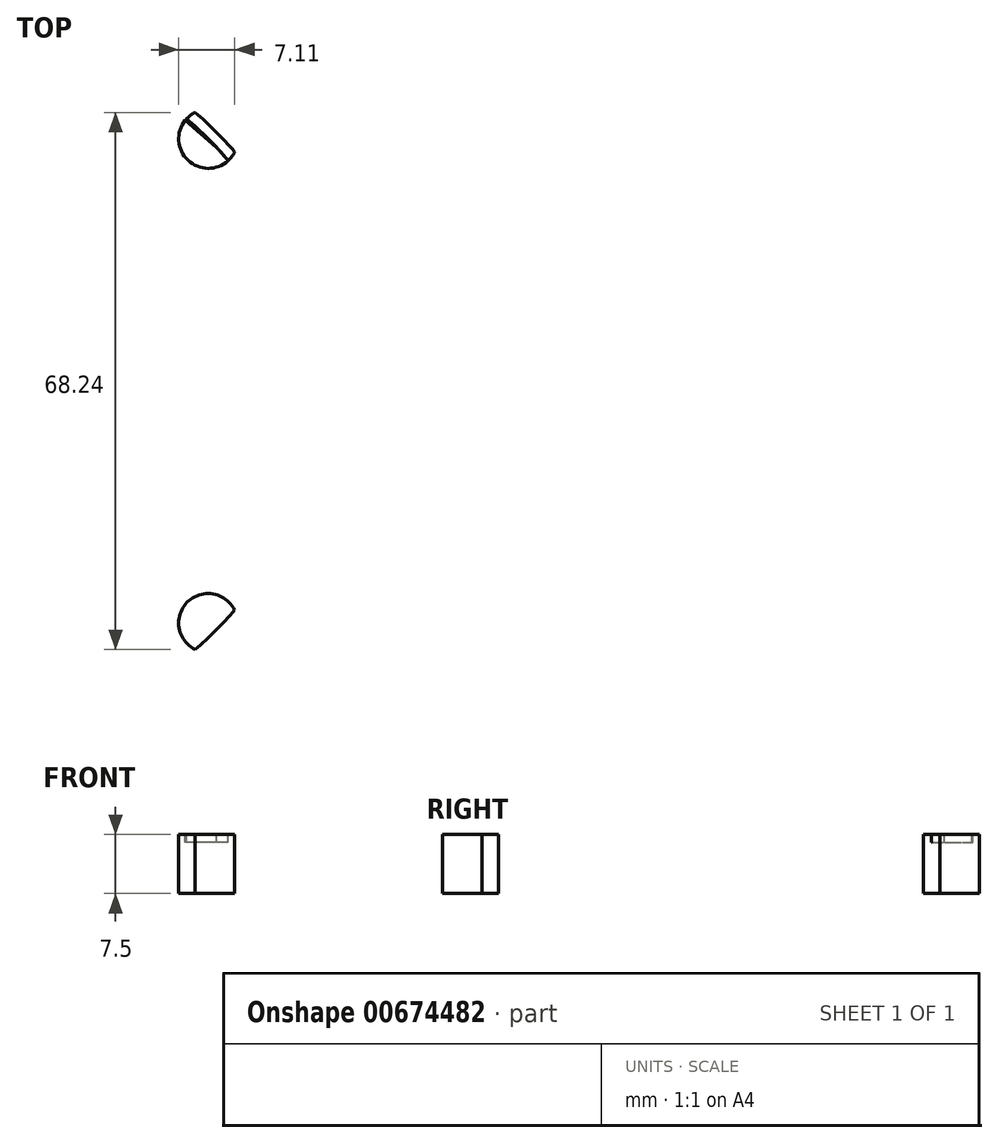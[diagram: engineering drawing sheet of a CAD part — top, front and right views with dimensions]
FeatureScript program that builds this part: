
annotation { "Feature Type Name" : "Feature", "Feature Type Description" : "" }
export const myFeature = defineFeature(function(context is Context, id is Id, definition is map)
    precondition{}
    {
        {
            var Q0;
            Q0=qCreatedBy(makeId("Top.planeOp"),FACE);
            var sketch = newSketch(context, id + "F0", { "sketchPlane" : qUnion([Q0])});
            skCircle(sketch, "E0", {"center": v(0, 0) * mm, "radius": 43.5 * mm, "construction": true});
            skLineSegment(sketch, "E1", {"start": v(0, 0) * mm, "end": v(30.76, 30.76) * mm, "construction": true});
            skCircle(sketch, "E2", {"center": v(30.76, 30.76) * mm, "radius": 3.75 * mm});
            skCircle(sketch, "E3.1.0", {"center": v(-30.76, 30.76) * mm, "radius": 3.75 * mm});
            skCircle(sketch, "E3.2.0", {"center": v(-30.76, -30.76) * mm, "radius": 3.75 * mm});
            skCircle(sketch, "E3.3.0", {"center": v(30.76, -30.76) * mm, "radius": 3.75 * mm});
            skLineSegment(sketch, "E4", {"start": v(0, 0) * mm, "end": v(30.76, -30.76) * mm, "construction": true});
            skSolve(sketch);
        }
        {
            var Q0;
            Q0=qCreatedBy(makeId("Top.planeOp"),FACE);
            var sketch = newSketch(context, id + "F1", { "sketchPlane" : qUnion([Q0])});
            skLineSegment(sketch, "E5", {"start": v(4.74, 19.78) * mm, "end": v(15.3, 42.68) * mm});
            skLineSegment(sketch, "E6", {"start": v(4.74, -19.78) * mm, "end": v(15.3, -42.68) * mm});
            skLineSegment(sketch, "E7", {"start": v(0, 0) * mm, "end": v(0, 47.02) * mm, "construction": true});
            skLineSegment(sketch, "E8", {"start": v(0, 0) * mm, "end": v(0, -46.33) * mm, "construction": true});
            skPoint(sketch, "E9.visualSharp", {"position": v(16.93, 46.23) * mm});
            skArc(sketch, "E9.filletArc", {"start": v(22.32, 38.88) * mm, "mid": v(20.83, 44.52) * mm, "end": v(15.3, 42.68) * mm});
            skPoint(sketch, "E10.visualSharp", {"position": v(4.23, 18.67) * mm});
            skArc(sketch, "E10.filletArc", {"start": v(4.74, 19.78) * mm, "mid": v(6.54, 14.55) * mm, "end": v(11.85, 16.11) * mm});
            skPoint(sketch, "E11.visualSharp", {"position": v(4.23, -18.67) * mm});
            skArc(sketch, "E11.filletArc", {"start": v(11.85, -16.11) * mm, "mid": v(6.54, -14.55) * mm, "end": v(4.74, -19.78) * mm});
            skPoint(sketch, "E12.visualSharp", {"position": v(16.93, -46.23) * mm});
            skArc(sketch, "E12.filletArc", {"start": v(15.3, -42.68) * mm, "mid": v(20.83, -44.52) * mm, "end": v(22.32, -38.88) * mm});
            skLineSegment(sketch, "E13", {"start": v(0, 0) * mm, "end": v(50, 0) * mm, "construction": true});
            skArc(sketch, "E14", {"start": v(11.85, 16.11) * mm, "mid": v(20, 0) * mm, "end": v(11.85, -16.11) * mm});
            skArc(sketch, "E15", {"start": v(22.32, 38.88) * mm, "mid": v(44.84, 0) * mm, "end": v(22.32, -38.88) * mm});
            skLineSegment(sketch, "E16", {"start": v(22.32, 38.88) * mm, "end": v(22.32, 0) * mm, "construction": true});
            skLineSegment(sketch, "E17", {"start": v(22.32, 0) * mm, "end": v(22.32, -38.88) * mm, "construction": true});
            skLineSegment(sketch, "E18", {"start": v(0, 42.68) * mm, "end": v(15.3, 42.68) * mm, "construction": true});
            skLineSegment(sketch, "E19", {"start": v(0, -42.68) * mm, "end": v(15.3, -42.68) * mm, "construction": true});
            skSolve(sketch);
        }
        {
            var Q0;
            Q0=makeQuery(id+"F1.imprint","IMPRINT",FACE,{"disambiguationData":[TD([[makeQuery(id+"F1.imprint","IMPRINT",EDGE,{"derivedFrom":sQuery(id+"F1.wireOp",EDGE,"E5")}),-1.0]])]});
            extrude(context, id + "F2", {"entities" : qUnion([Q0]), "depth" : 3 * mm, "offsetDistance" : 25 * mm});
        }
        {
            var Q0;
            Q0=makeQuery(id+"F0.imprint","IMPRINT",FACE,{"disambiguationData":[TD([[makeQuery(id+"F0.imprint","IMPRINT",EDGE,{"derivedFrom":sQuery(id+"F0.wireOp",EDGE,"E2")}),1.0]])]});
            var Q1;
            Q1=makeQuery(id+"F0.imprint","IMPRINT",FACE,{"disambiguationData":[TD([[makeQuery(id+"F0.imprint","IMPRINT",EDGE,{"derivedFrom":sQuery(id+"F0.wireOp",EDGE,"E3.3.0")}),1.0]])]});
            extrude(context, id + "F3", {"entities" : qUnion([Q0, Q1]), "operationType" : NewBodyOperationType.REMOVE, "depth" : 25 * mm, "offsetDistance" : 25 * mm});
        }
        {
            var Q0;
            Q0=makeQuery(id+"F2.opExtrude","CAP_FACE",FACE,{"disambiguationData":[OSD([sQuery(id+"F1.wireOp",EDGE,"KiuFZQME-wWnU-ktu5-Gd9x-qji5TMNZz2fd"),sQuery(id+"F1.wireOp",EDGE,"G5eraXv0-ftC7-V2Hx-4i3N-1R2XA50WnSdq"),sQuery(id+"F1.wireOp",EDGE,"E5"),sQuery(id+"F1.wireOp",EDGE,"E6"),sQuery(id+"F1.wireOp",EDGE,"57560024-62e8-479f-91f4-8b403f4d0ad7.filletArc"),sQuery(id+"F1.wireOp",EDGE,"ddf71622-e854-4fa8-aca5-087326283111.filletArc"),sQuery(id+"F1.wireOp",EDGE,"85b82a5b-4425-4996-801d-5779b438c59f.filletArc"),sQuery(id+"F1.wireOp",EDGE,"35c327b1-5974-4460-b54d-dc77ba413df5.filletArc")])],"isStart":false});
            var sketch = newSketch(context, id + "F4", { "sketchPlane" : qUnion([Q0])});
            skArc(sketch, "E20", {"start": v(13.6, 20.4) * mm, "mid": v(24.52, 0) * mm, "end": v(13.6, -20.4) * mm});
            skArc(sketch, "E21", {"start": v(16.92, 25.4) * mm, "mid": v(30.52, 0) * mm, "end": v(16.92, -25.4) * mm});
            skLineSegment(sketch, "E22", {"start": v(0, 0) * mm, "end": v(16.92, -25.4) * mm, "construction": true});
            skLineSegment(sketch, "E23", {"start": v(0, 0) * mm, "end": v(16.92, 25.4) * mm, "construction": true});
            skLineSegment(sketch, "E24", {"start": v(13.6, 20.4) * mm, "end": v(13.6, 0) * mm, "construction": true});
            skLineSegment(sketch, "E25", {"start": v(13.6, 0) * mm, "end": v(13.6, -20.4) * mm, "construction": true});
            skArc(sketch, "E26", {"start": v(13.6, 20.4) * mm, "mid": v(12.76, 24.57) * mm, "end": v(16.92, 25.4) * mm});
            skArc(sketch, "E27", {"start": v(13.6, -20.4) * mm, "mid": v(12.76, -24.57) * mm, "end": v(16.92, -25.4) * mm});
            skSolve(sketch);
        }
        {
            var Q0;
            Q0=qSketchRegion(id+"F4",true);
            extrude(context, id + "F5", {"entities" : qUnion([Q0]), "operationType" : NewBodyOperationType.REMOVE, "oppositeDirection" : true, "depth" : 25 * mm, "offsetDistance" : 25 * mm});
        }
        {
            var Q0;
            Q0=makeQuery(id+"F2.opExtrude","CAP_FACE",FACE,{"disambiguationData":[OSD([sQuery(id+"F1.wireOp",EDGE,"E5"),sQuery(id+"F1.wireOp",EDGE,"E6"),sQuery(id+"F1.wireOp",EDGE,"E9.filletArc"),sQuery(id+"F1.wireOp",EDGE,"E10.filletArc"),sQuery(id+"F1.wireOp",EDGE,"E11.filletArc"),sQuery(id+"F1.wireOp",EDGE,"E12.filletArc"),sQuery(id+"F1.wireOp",EDGE,"E14"),sQuery(id+"F1.wireOp",EDGE,"E15")])],"isStart":true});
            var sketch = newSketch(context, id + "F6", { "sketchPlane" : qUnion([Q0])});
            skArc(sketch, "E28", {"start": v(22.32, -38.88) * mm, "mid": v(44.66, 3.97) * mm, "end": v(15.12, 42.21) * mm});
            skArc(sketch, "E29", {"start": v(11.26, 24.36) * mm, "mid": v(26.84, 0) * mm, "end": v(11.26, -24.36) * mm});
            skLineSegment(sketch, "E30", {"start": v(9.3, -29.67) * mm, "end": v(15.3, -42.68) * mm});
            skLineSegment(sketch, "E31", {"start": v(9.3, 29.67) * mm, "end": v(15.3, 42.68) * mm});
            skArc(sketch, "E32", {"start": v(15.3, -42.68) * mm, "mid": v(20.83, -44.52) * mm, "end": v(22.32, -38.88) * mm});
            skArc(sketch, "E33", {"start": v(15.12, 42.21) * mm, "mid": v(14.97, 42.54) * mm, "end": v(15.3, 42.68) * mm});
            skPoint(sketch, "E34.visualSharp", {"position": v(7.5, -25.77) * mm});
            skArc(sketch, "E34.filletArc", {"start": v(11.26, -24.36) * mm, "mid": v(9.18, -26.61) * mm, "end": v(9.3, -29.67) * mm});
            skPoint(sketch, "E35.visualSharp", {"position": v(7.5, 25.77) * mm});
            skArc(sketch, "E35.filletArc", {"start": v(9.3, 29.67) * mm, "mid": v(9.18, 26.61) * mm, "end": v(11.26, 24.36) * mm});
            skSolve(sketch);
        }
        {
            var Q0;
            Q0=makeQuery(id+"F6.imprint","IMPRINT",FACE,{"disambiguationData":[TD([[makeQuery(id+"F6.imprint","IMPRINT",EDGE,{"derivedFrom":sQuery(id+"F6.wireOp",EDGE,"E28")}),1.0]])]});
            extrude(context, id + "F7", {"entities" : qUnion([Q0]), "depth" : 7.5 * mm, "offsetDistance" : 25 * mm});
        }
        {
            var Q0;
            Q0=makeQuery(id+"F2.opExtrude","SWEPT_BODY",BODY,{"disambiguationData":[OSD([sQuery(id+"F1.wireOp",EDGE,"E5"),sQuery(id+"F1.wireOp",EDGE,"E6"),sQuery(id+"F1.wireOp",EDGE,"E9.filletArc"),sQuery(id+"F1.wireOp",EDGE,"E10.filletArc"),sQuery(id+"F1.wireOp",EDGE,"E11.filletArc"),sQuery(id+"F1.wireOp",EDGE,"E12.filletArc"),sQuery(id+"F1.wireOp",EDGE,"E14"),sQuery(id+"F1.wireOp",EDGE,"E15")])]});
            deleteBodies(context, id + "F8", {"entities" : qUnion([Q0])});
        }
        {
            var Q0;
            Q0=makeQuery(id+"F7.opExtrude","CAP_FACE",FACE,{"disambiguationData":[OSD([sQuery(id+"F0.wireOp",EDGE,"E2"),sQuery(id+"F0.wireOp",EDGE,"E3.3.0"),sQuery(id+"F6.wireOp",EDGE,"E28"),sQuery(id+"F6.wireOp",EDGE,"E29"),sQuery(id+"F6.wireOp",EDGE,"E30"),sQuery(id+"F6.wireOp",EDGE,"E31"),sQuery(id+"F6.wireOp",EDGE,"E32"),sQuery(id+"F6.wireOp",EDGE,"E33"),sQuery(id+"F6.wireOp",EDGE,"E34.filletArc"),sQuery(id+"F6.wireOp",EDGE,"E35.filletArc")])],"isStart":true});
            var sketch = newSketch(context, id + "F9", { "sketchPlane" : qUnion([Q0])});
            skArc(sketch, "E36", {"start": v(31.8, 29.67) * mm, "mid": v(33.09, 28.23) * mm, "end": v(34.3, 26.73) * mm});
            skArc(sketch, "E37", {"start": v(25.11, 35.53) * mm, "mid": v(30.24, 31.28) * mm, "end": v(34.66, 26.3) * mm});
            skCircle(sketch, "E38", {"center": v(30.76, 30.76) * mm, "radius": 3.75 * mm, "construction": true});
            skLineSegment(sketch, "E39", {"start": v(30.75, 30.76) * mm, "end": v(30.76, 30.76) * mm, "construction": true});
            skLineSegment(sketch, "E40", {"start": v(30.76, 30.76) * mm, "end": v(30.77, 30.76) * mm, "construction": true});
            skLineSegment(sketch, "E41", {"start": v(31.8, 29.67) * mm, "end": v(25.11, 35.53) * mm});
            skLineSegment(sketch, "E42", {"start": v(34.3, 26.73) * mm, "end": v(34.66, 26.3) * mm});
            skSolve(sketch);
        }
        {
            var Q0;
            Q0 = qSketchRegion(id + "F9", true);
            extrude(context, id + "F10", {"entities" : qUnion([Q0]), "operationType" : NewBodyOperationType.REMOVE, "oppositeDirection" : true, "depth" : 1 * mm, "offsetDistance" : 25 * mm});
        }
    });
